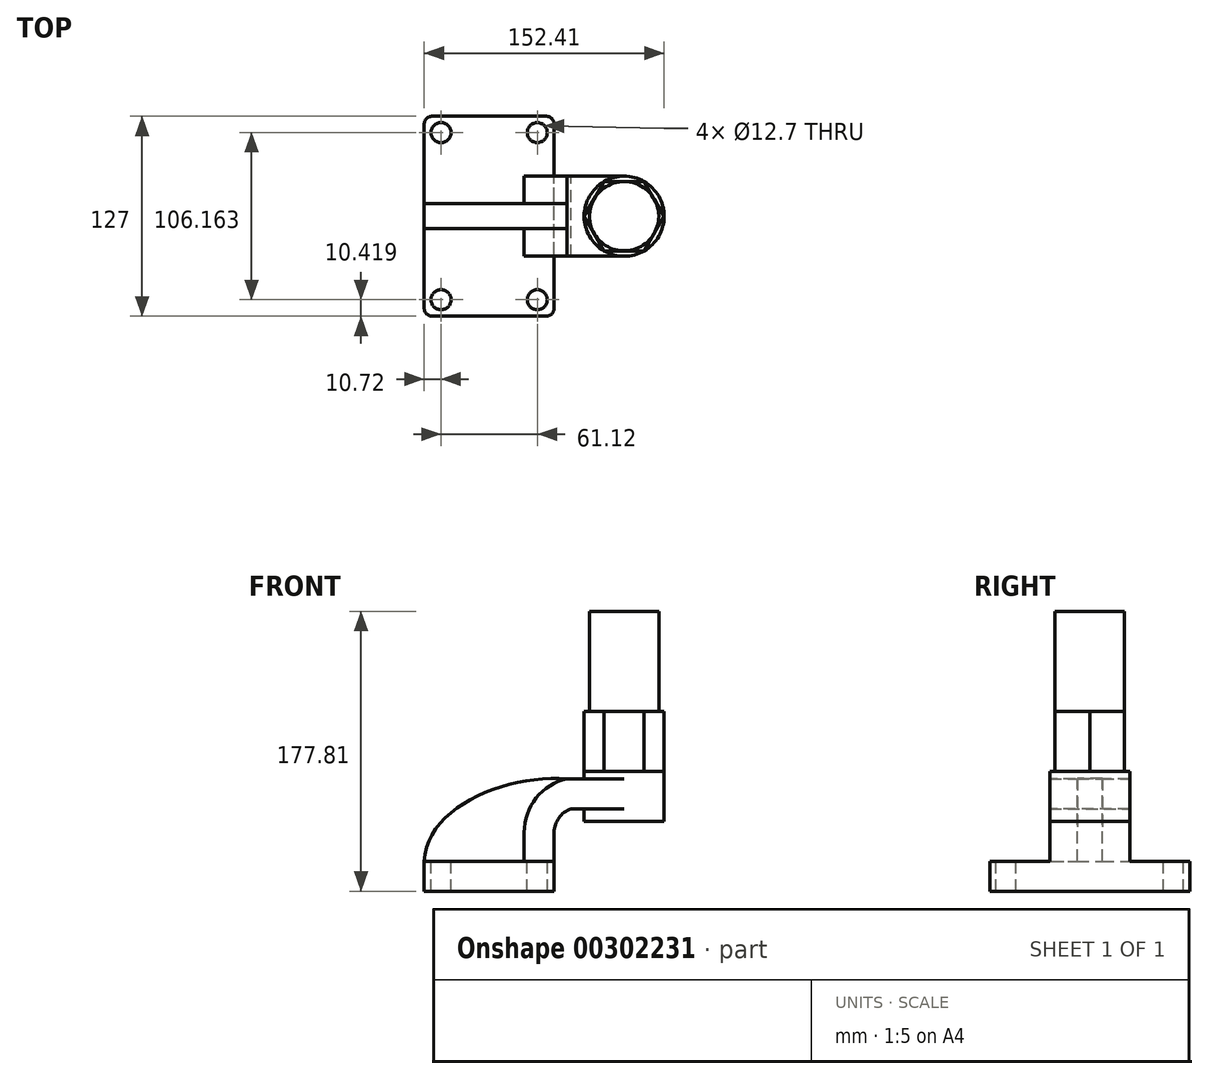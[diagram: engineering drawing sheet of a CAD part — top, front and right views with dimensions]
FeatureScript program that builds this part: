
annotation { "Feature Type Name" : "Feature", "Feature Type Description" : "" }
export const myFeature = defineFeature(function(context is Context, id is Id, definition is map)
    precondition{}
    {
        {
            var Q0;
            Q0=qCreatedBy(makeId("Front.planeOp"),FACE);
            var sketch = newSketch(context, id + "F0", { "sketchPlane" : qUnion([Q0])});
            skLineSegment(sketch, "E0.bottom", {"start": v(-41.28, -9.53) * mm, "end": v(41.28, -9.53) * mm});
            skLineSegment(sketch, "E0.top", {"start": v(-41.28, 9.53) * mm, "end": v(41.28, 9.53) * mm});
            skLineSegment(sketch, "E0.left", {"start": v(-41.28, -9.53) * mm, "end": v(-41.28, 9.53) * mm});
            skLineSegment(sketch, "E0.right", {"start": v(41.28, -9.53) * mm, "end": v(41.28, 9.53) * mm});
            skPoint(sketch, "E0.middle", {"position": v(0, 0) * mm});
            skLineSegment(sketch, "E1.bottom", {"start": v(60.33, 34.93) * mm, "end": v(111.12, 34.93) * mm});
            skLineSegment(sketch, "E1.top", {"start": v(60.33, 66.67) * mm, "end": v(111.12, 66.67) * mm});
            skLineSegment(sketch, "E1.left", {"start": v(60.33, 34.93) * mm, "end": v(60.32, 66.67) * mm});
            skLineSegment(sketch, "E1.right", {"start": v(111.12, 34.93) * mm, "end": v(111.12, 66.68) * mm});
            skPoint(sketch, "E1.middle", {"position": v(85.72, 50.8) * mm});
            skLineSegment(sketch, "E2", {"start": v(41.27, 9.52) * mm, "end": v(41.27, 27.83) * mm});
            skArc(sketch, "E3", {"start": v(41.27, 27.83) * mm, "mid": v(44.26, 37.1) * mm, "end": v(52.1, 42.88) * mm});
            skLineSegment(sketch, "E4", {"start": v(52.1, 42.88) * mm, "end": v(85.72, 42.88) * mm});
            skLineSegment(sketch, "E5.0", {"start": v(22.22, 9.52) * mm, "end": v(22.22, 27.83) * mm});
            skArc(sketch, "E6.0", {"start": v(22.22, 27.83) * mm, "mid": v(29.91, 49.69) * mm, "end": v(49.6, 61.93) * mm});
            skLineSegment(sketch, "E7.0", {"start": v(49.6, 61.93) * mm, "end": v(85.72, 61.93) * mm});
            skFitSpline(sketch, "E8", {"points": [v(-41.28, 9.53) * mm, v(49.6, 61.93) * mm], "startDerivative": vector(5.1, 105.04) * mm, "endDerivative": vector(116.3, -8) * mm});
            skLineSegment(sketch, "E9", {"start": v(22.22, 9.52) * mm, "end": v(41.28, 9.53) * mm});
            skLineSegment(sketch, "E10", {"start": v(85.72, 61.93) * mm, "end": v(85.72, 42.88) * mm});
            skLineSegment(sketch, "E11", {"start": v(85.72, 66.67) * mm, "end": v(85.72, 34.93) * mm});
            skSolve(sketch);
        }
        {
            var Q0;
            Q0=makeQuery(id+"F0.imprint","IMPRINT",FACE,{"disambiguationData":[TD([[makeQuery(id+"F0.imprint","IMPRINT",EDGE,{"derivedFrom":sQuery(id+"F0.wireOp",EDGE,"E0.bottom")}),1.0]])]});
            extrude(context, id + "F1", {"entities" : qUnion([Q0]), "endBound" : BoundingType.SYMMETRIC, "depth" : 127 * mm});
        }
        {
            var Q0;
            Q0=makeQuery(id+"F0.imprint","IMPRINT",FACE,{"disambiguationData":[TD([[makeQuery(id+"F0.imprint","IMPRINT",EDGE,{"derivedFrom":sQuery(id+"F0.wireOp",EDGE,"E2")}),1.0]])]});
            var Q1;
            {var subQ0=sQuery(id+"F0.wireOp",EDGE,"E4");var subQ1=sQuery(id+"F0.wireOp",EDGE,"E1.left");var subQ2=makeQuery(id+"F0.imprint","INTERSECT",VERTEX,{"derivedFrom":[subQ1,subQ0]});Q1=makeQuery(id+"F0.imprint","IMPRINT",FACE,{"disambiguationData":[TD([[makeQuery(id+"F0.imprint","IMPRINT",EDGE,{"disambiguationData":[TD([[subQ2,-1.0]])],"derivedFrom":subQ1}),-1.0]])]});}
            extrude(context, id + "F2", {"entities" : qUnion([Q0, Q1]), "endBound" : BoundingType.SYMMETRIC, "depth" : 50.8 * mm});
        }
        {
            var Q0;
            Q0=makeQuery(id+"F0.imprint","IMPRINT",FACE,{"disambiguationData":[TD([[makeQuery(id+"F0.imprint","IMPRINT",EDGE,{"derivedFrom":sQuery(id+"F0.wireOp",EDGE,"E0.top")}),1.0]])]});
            extrude(context, id + "F3", {"entities" : qUnion([Q0]), "operationType" : NewBodyOperationType.ADD, "endBound" : BoundingType.SYMMETRIC, "depth" : 15.88 * mm});
        }
        {
            var Q0;
            {var subQ0=sQuery(id+"F0.wireOp",EDGE,"E1.right");Q0=makeQuery(id+"F0.imprint","IMPRINT",FACE,{"disambiguationData":[TD([[makeQuery(id+"F0.imprint","IMPRINT",EDGE,{"derivedFrom":subQ0}),1.0]])]});}
            var Q1;
            Q1=sQuery(id+"F0.wireOp",EDGE,"E11");
            revolve(context, id + "F4", {"operationType" : NewBodyOperationType.ADD, "entities" : qUnion([Q0]), "axis" : qUnion([Q1]), "revolveType" : RevolveType.FULL});
        }
        {
            var Q0;
            Q0=makeQuery(id+"F1.opExtrude","CAP_EDGE",EDGE,{"disambiguationData":[OSD([sQuery(id+"F0.wireOp",EDGE,"E0.right")])],"isStart":false});
            var Q1;
            Q1=makeQuery(id+"F1.opExtrude","CAP_EDGE",EDGE,{"disambiguationData":[OSD([sQuery(id+"F0.wireOp",EDGE,"E0.left")])],"isStart":false});
            var Q2;
            Q2=makeQuery(id+"F1.opExtrude","CAP_EDGE",EDGE,{"disambiguationData":[OSD([sQuery(id+"F0.wireOp",EDGE,"E0.right")])],"isStart":true});
            var Q3;
            Q3=makeQuery(id+"F1.opExtrude","CAP_EDGE",EDGE,{"disambiguationData":[OSD([sQuery(id+"F0.wireOp",EDGE,"E0.left")])],"isStart":true});
            fillet(context, id + "F5", {"entities" : qUnion([Q0, Q1, Q2, Q3]), "radius" : 5.08 * mm, "tangentPropagation" : true, "allowEdgeOverflow" : false});
        }
        {
            var Q0;
            Q0=qCreatedBy(makeId("Top.planeOp"),FACE);
            var sketch = newSketch(context, id + "F6", { "sketchPlane" : qUnion([Q0])});
            skCircle(sketch, "E12", {"center": v(30.56, -53.08) * mm, "radius": 6.35 * mm});
            skCircle(sketch, "E13.MirrorC", {"center": v(-30.56, -53.08) * mm, "radius": 6.35 * mm});
            skCircle(sketch, "E14.MirrorC", {"center": v(-30.56, 53.08) * mm, "radius": 6.35 * mm});
            skCircle(sketch, "E15.MirrorC", {"center": v(30.56, 53.08) * mm, "radius": 6.35 * mm});
            skSolve(sketch);
        }
        {
            var Q0;
            Q0=sQuery(id+"F6.wireOp",VERTEX,"E15.MirrorC.center");
            var Q1;
            Q1=sQuery(id+"F6.wireOp",VERTEX,"E14.MirrorC.center");
            var Q2;
            Q2=sQuery(id+"F6.wireOp",VERTEX,"E13.MirrorC.center");
            var Q3;
            Q3=sQuery(id+"F6.wireOp",VERTEX,"E12.center");
            var Q4;
            Q4=makeQuery(id+"F1.opExtrude","SWEPT_BODY",BODY,{"disambiguationData":[OSD([sQuery(id+"F0.wireOp",EDGE,"E0.bottom"),sQuery(id+"F0.wireOp",EDGE,"E0.top"),sQuery(id+"F0.wireOp",EDGE,"E0.left"),sQuery(id+"F0.wireOp",EDGE,"E0.right"),sQuery(id+"F0.wireOp",EDGE,"E9")])]});
            hole(context, id + "F7", {"style" : HoleStyle.SIMPLE, "endStyle" : HoleEndStyle.THROUGH, "holeDiameter" : 12.7 * mm, "tappedDepth" : 12.7 * mm, "tapClearance" : 3, "startFromSketch" : true, "locations" : qUnion([Q0, Q1, Q2, Q3]), "scope" : qUnion([Q4])});
        }
        {
            var Q0;
            Q0=sQuery(id+"F6.wireOp",VERTEX,"E14.MirrorC.center");
            var Q1;
            Q1=sQuery(id+"F6.wireOp",VERTEX,"E15.MirrorC.center");
            var Q2;
            Q2=sQuery(id+"F6.wireOp",VERTEX,"E13.MirrorC.center");
            var Q3;
            Q3=sQuery(id+"F6.wireOp",VERTEX,"E12.center");
            var Q4;
            Q4=makeQuery(id+"F1.opExtrude","SWEPT_BODY",BODY,{"disambiguationData":[OSD([sQuery(id+"F0.wireOp",EDGE,"E0.bottom"),sQuery(id+"F0.wireOp",EDGE,"E0.top"),sQuery(id+"F0.wireOp",EDGE,"E0.left"),sQuery(id+"F0.wireOp",EDGE,"E0.right"),sQuery(id+"F0.wireOp",EDGE,"E9")])]});
            hole(context, id + "F8", {"style" : HoleStyle.SIMPLE, "endStyle" : HoleEndStyle.THROUGH, "oppositeDirection" : true, "holeDiameter" : 12.7 * mm, "tappedDepth" : 12.7 * mm, "tapClearance" : 3, "locations" : qUnion([Q0, Q1, Q2, Q3]), "scope" : qUnion([Q4])});
        }
        {
            var Q0;
            Q0=makeQuery(id+"F4.opRevolve","SWEPT_FACE",FACE,{"disambiguationData":[OSD([sQuery(id+"F0.wireOp",EDGE,"E1.top")])]});
            var sketch = newSketch(context, id + "F9", { "sketchPlane" : qUnion([Q0])});
            skCircle(sketch, "E16.cCircle", {"center": v(85.72, 0) * mm, "radius": 25.4 * mm, "construction": true});
            skLineSegment(sketch, "E16.0", {"start": v(111.12, 0) * mm, "end": v(98.42, -22) * mm});
            skLineSegment(sketch, "E16.1", {"start": v(98.42, -22) * mm, "end": v(73.02, -22) * mm});
            skLineSegment(sketch, "E16.2", {"start": v(73.02, -22) * mm, "end": v(60.32, 0) * mm});
            skLineSegment(sketch, "E16.3", {"start": v(60.32, 0) * mm, "end": v(73.02, 22) * mm});
            skLineSegment(sketch, "E16.4", {"start": v(73.02, 22) * mm, "end": v(98.42, 22) * mm});
            skLineSegment(sketch, "E16.5", {"start": v(98.42, 22) * mm, "end": v(111.12, 0) * mm});
            skSolve(sketch);
        }
        {
            var Q0;
            Q0=makeQuery(id+"F9.imprint","IMPRINT",FACE,{"disambiguationData":[TD([[makeQuery(id+"F9.imprint","IMPRINT",EDGE,{"derivedFrom":sQuery(id+"F9.wireOp",EDGE,"E16.0")}),-1.0]])]});
            extrude(context, id + "F10", {"entities" : qUnion([Q0]), "operationType" : NewBodyOperationType.ADD, "depth" : 38.1 * mm});
        }
        {
            var Q0;
            Q0=makeQuery(id+"F10.opExtrude","CAP_FACE",FACE,{"disambiguationData":[OSD([sQuery(id+"F9.wireOp",EDGE,"E16.0"),sQuery(id+"F9.wireOp",EDGE,"E16.1"),sQuery(id+"F9.wireOp",EDGE,"E16.2"),sQuery(id+"F9.wireOp",EDGE,"E16.3"),sQuery(id+"F9.wireOp",EDGE,"E16.4"),sQuery(id+"F9.wireOp",EDGE,"E16.5")])],"isStart":false});
            var sketch = newSketch(context, id + "F11", { "sketchPlane" : qUnion([Q0])});
            skCircle(sketch, "E17", {"center": v(85.72, 0) * mm, "radius": 22 * mm});
            skPoint(sketch, "E17.centerSnap0", {"position": v(85.72, -22) * mm});
            skSolve(sketch);
        }
        {
            var Q0;
            Q0 = qSketchRegion(id + "F11", true);
            extrude(context, id + "F12", {"entities" : qUnion([Q0]), "operationType" : NewBodyOperationType.ADD, "depth" : 63.5 * mm});
        }
    });
